# Revit family: 61019 Велопарковка «Локус» Хоббика
name_source: partatom
category: Антураж
revit_build: Autodesk Revit 2018 (Build: 20180423_1000(x64)
units: mm (PartAtom-declared; Revit-internal decimal feet)

## family parameters
Всегда вертикально = Да
Источник визуального образа = Геометрия семейства
На основе рабочей плоскости = Нет
Общий = Нет
При загрузке вырезать с полостями = Нет
Точка расчета площади = Нет

## types (3) — shared parameters
URL = https://hobbyka.ru
Артикул товара = Арт. 61019
Высота = 660 мм
Группа модели = Велопарковки
Изготовитель = ООО «Хоббика»
Изображение типоразмера = Велопарковка «Локус» Арт 61019.jpg
Материал изделия = Сталь
Цвет каркаса = Сталь
Ширина = 550 мм

## per-type parameters (varying)
| type | 11 мест | 17 мест | 7 мест | Длина | Кол-во мест | Описание |
| 7 мест | Нет | Нет | Да | 3360 мм | 6 | Велопарковка «Локус». Версия на 7 мест |
| 11 мест | Да | Нет | Нет | 4820 мм | 10 | Велопарковка «Локус». Версия на 11 мест |
| 17 мест | Нет | Да | Нет | 7000 мм | 16 | Велопарковка «Локус». Версия на 17 мест |
